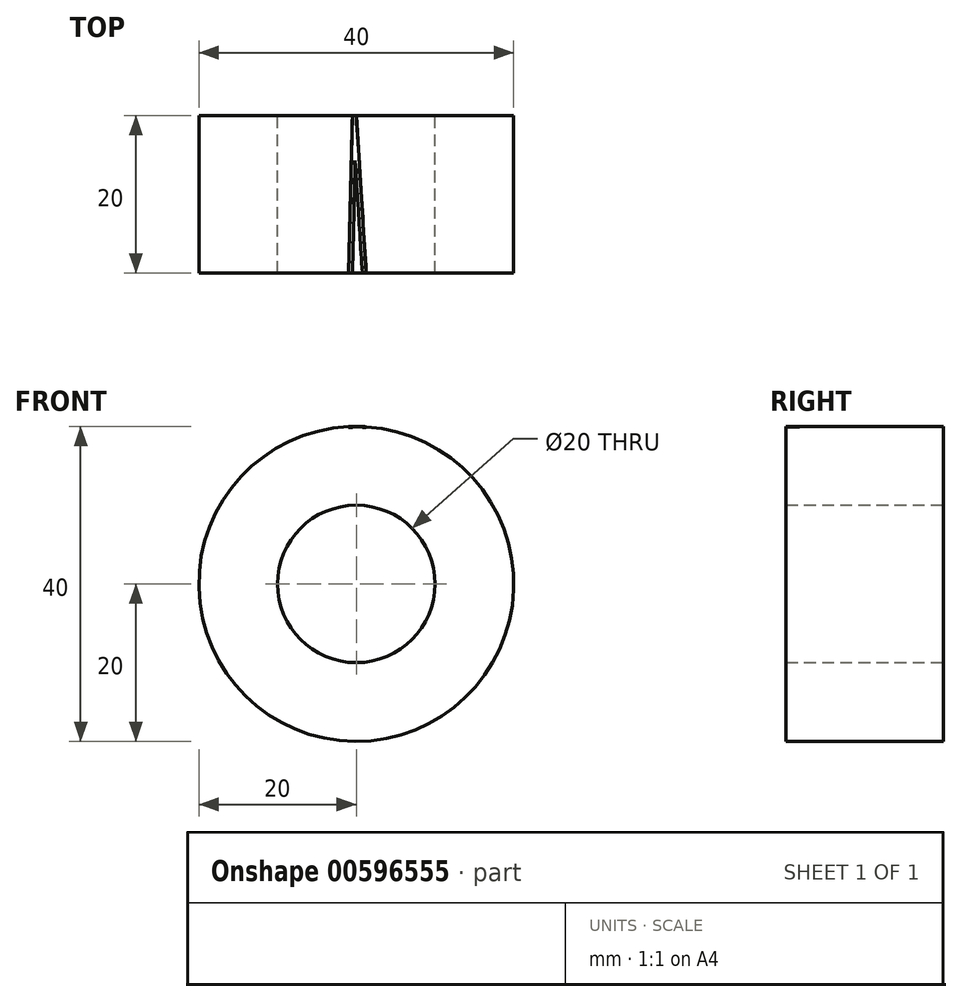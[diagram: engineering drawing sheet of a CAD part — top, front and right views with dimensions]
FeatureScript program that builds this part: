
annotation { "Feature Type Name" : "Feature", "Feature Type Description" : "" }
export const myFeature = defineFeature(function(context is Context, id is Id, definition is map)
    precondition{}
    {
        {
            var Q0;
            Q0=qCreatedBy(makeId("Front.planeOp"),FACE);
            var sketch = newSketch(context, id + "F0", { "sketchPlane" : qUnion([Q0])});
            skCircle(sketch, "E0", {"center": v(0, 0) * mm, "radius": 20 * mm});
            skCircle(sketch, "E1", {"center": v(0, 0) * mm, "radius": 10 * mm});
            skSolve(sketch);
        }
        {
            var Q0;
            Q0=makeQuery(id+"F0.imprint","IMPRINT",FACE,{"disambiguationData":[TD([[makeQuery(id+"F0.imprint","IMPRINT",EDGE,{"derivedFrom":sQuery(id+"F0.wireOp",EDGE,"E0")}),1.0]])]});
            extrude(context, id + "F1", {"entities" : qUnion([Q0]), "depth" : 20 * mm, "offsetDistance" : 25 * mm});
        }
        {
            var Q0;
            Q0=qCreatedBy(makeId("Top.planeOp"),FACE);
            cPlane(context, id + "F2", {"entities" : qUnion([Q0]), "cplaneType" : CPlaneType.OFFSET, "offset" : 20 * mm, "width" : 150 * mm, "height" : 150 * mm});
        }
        {
            var Q0;
            Q0=qCreatedBy(id+"F2.planeOp",FACE);
            var sketch = newSketch(context, id + "F3", { "sketchPlane" : qUnion([Q0])});
            skLineSegment(sketch, "E2", {"start": v(0, 0) * mm, "end": v(1.27, -20) * mm});
            skLineSegment(sketch, "E3.0", {"start": v(-0.5, 0) * mm, "end": v(0.76, -20) * mm});
            skLineSegment(sketch, "E4", {"start": v(-0.5, 0) * mm, "end": v(0, 0) * mm});
            skLineSegment(sketch, "E5", {"start": v(1.27, -20) * mm, "end": v(0.76, -20) * mm});
            skSolve(sketch);
        }
        {
            var Q0;
            Q0 = qSketchRegion(id + "F3", true);
            extrude(context, id + "F4", {"entities" : qUnion([Q0]), "operationType" : NewBodyOperationType.REMOVE, "oppositeDirection" : true, "depth" : .1 * mm, "offsetDistance" : 25 * mm});
        }
        {
            var Q0;
            Q0=qCreatedBy(id+"F2.planeOp",FACE);
            var sketch = newSketch(context, id + "F5", { "sketchPlane" : qUnion([Q0])});
            skLineSegment(sketch, "E6", {"start": v(0, 0) * mm, "end": v(-0.48, -20) * mm});
            skLineSegment(sketch, "E7.0", {"start": v(-0.5, 0.01) * mm, "end": v(-0.98, -20) * mm});
            skLineSegment(sketch, "E8", {"start": v(-0.98, -20) * mm, "end": v(-0.48, -20) * mm});
            skLineSegment(sketch, "E9", {"start": v(-0.5, 0.01) * mm, "end": v(0, 0) * mm});
            skSolve(sketch);
        }
        {
            var Q0;
            Q0 = qSketchRegion(id + "F5", true);
            extrude(context, id + "F6", {"entities" : qUnion([Q0]), "operationType" : NewBodyOperationType.REMOVE, "oppositeDirection" : true, "depth" : 0.1 * mm, "offsetDistance" : 25 * mm});
        }
    });
